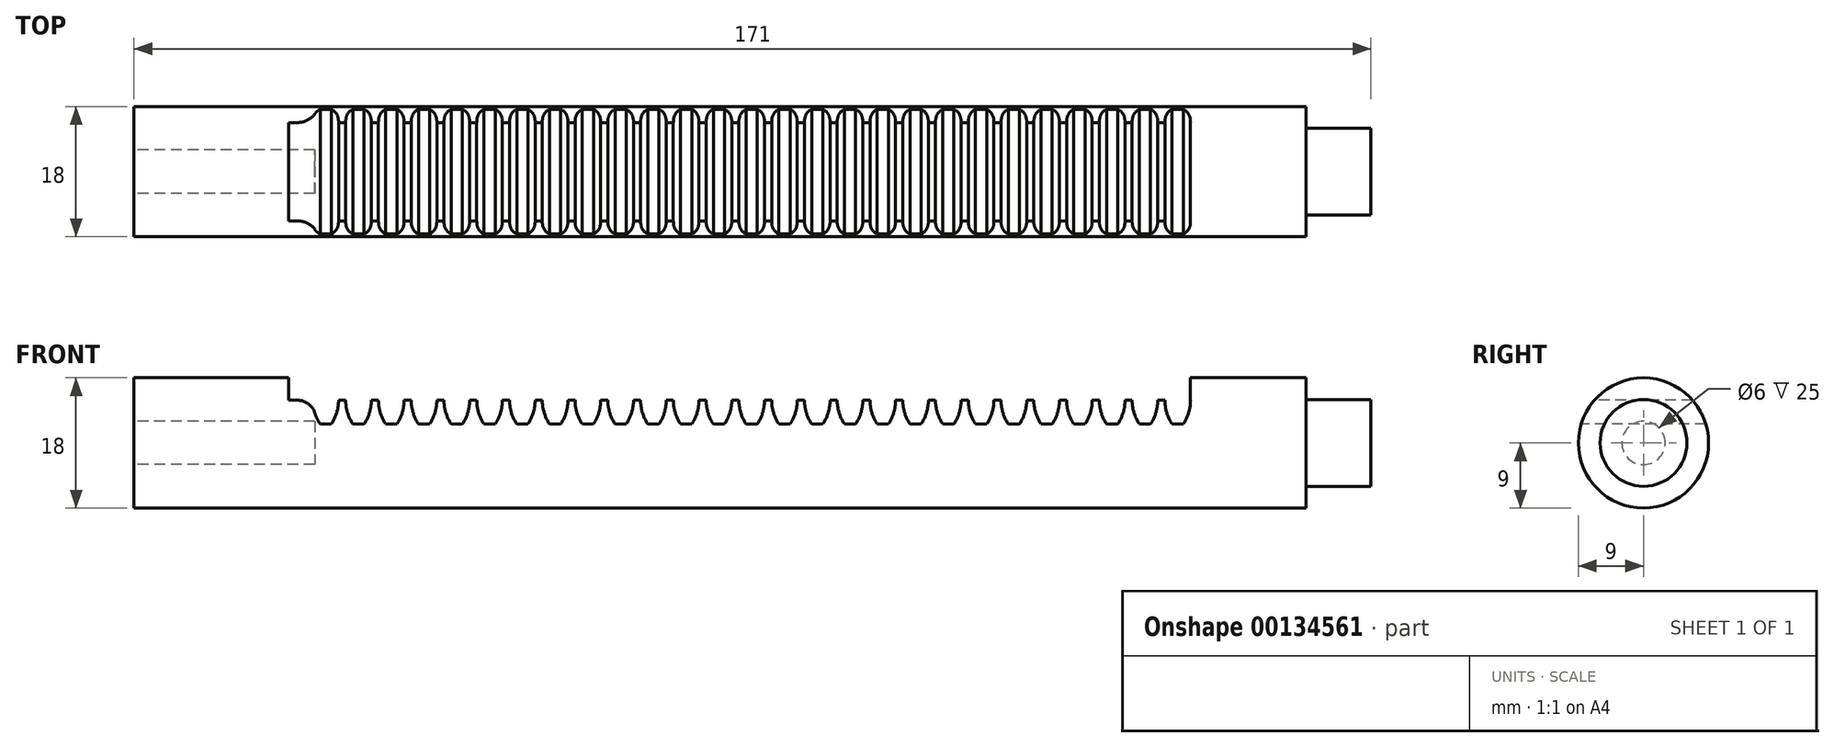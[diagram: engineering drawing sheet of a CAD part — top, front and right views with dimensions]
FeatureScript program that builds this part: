
annotation { "Feature Type Name" : "Feature", "Feature Type Description" : "" }
export const myFeature = defineFeature(function(context is Context, id is Id, definition is map)
    precondition{}
    {
        {
            var Q0;
            Q0=qCreatedBy(makeId("Right.planeOp"),FACE);
            var sketch = newSketch(context, id + "F0", { "sketchPlane" : qUnion([Q0])});
            skCircle(sketch, "E0", {"center": v(0, 0) * mm, "radius": 9 * mm});
            skSolve(sketch);
        }
        {
            var Q0;
            Q0 = qSketchRegion(id + "F0", true);
            extrude(context, id + "F1", {"entities" : qUnion([Q0]), "oppositeDirection" : true, "depth" : 162 * mm});
        }
        {
            var Q0;
            Q0=qCreatedBy(makeId("Front.planeOp"),FACE);
            var sketch = newSketch(context, id + "F2", { "sketchPlane" : qUnion([Q0])});
            skLineSegment(sketch, "E1.0", {"start": v(-162, 9) * mm, "end": v(-162, -9) * mm});
            skLineSegment(sketch, "E2", {"start": v(-162, 9) * mm, "end": v(0, 9) * mm});
            skLineSegment(sketch, "E3.0", {"start": v(0, 9) * mm, "end": v(0, -9) * mm});
            skLineSegment(sketch, "E4", {"start": v(-162, 2.6) * mm, "end": v(0, 2.6) * mm, "construction": true});
            skLineSegment(sketch, "E5", {"start": v(-162, 5.9) * mm, "end": v(0, 5.9) * mm});
            skLineSegment(sketch, "E6", {"start": v(-140.6, 5.9) * mm, "end": v(-140.6, 9) * mm});
            skPoint(sketch, "E7", {"position": v(-137.28, 5.9) * mm});
            skArc(sketch, "E8", {"start": v(-137.28, 5.9) * mm, "mid": v(-137.02, 4.18) * mm, "end": v(-136.28, 2.6) * mm});
            skLineSegment(sketch, "E9", {"start": v(-135.5, 8.15) * mm, "end": v(-135.5, -2.56) * mm, "construction": true});
            skArc(sketch, "E10.MirrorCS", {"start": v(-133.73, 5.9) * mm, "mid": v(-133.98, 4.18) * mm, "end": v(-134.73, 2.6) * mm});
            skLineSegment(sketch, "E11", {"start": v(-134.73, 2.6) * mm, "end": v(-136.28, 2.6) * mm});
            skArc(sketch, "E12.1.0.0", {"start": v(-132.75, 5.9) * mm, "mid": v(-132.49, 4.18) * mm, "end": v(-131.75, 2.6) * mm});
            skArc(sketch, "E12.1.0.1", {"start": v(-129.2, 5.9) * mm, "mid": v(-129.45, 4.18) * mm, "end": v(-130.2, 2.6) * mm});
            skArc(sketch, "E12.2.0.0", {"start": v(-128.22, 5.9) * mm, "mid": v(-127.96, 4.18) * mm, "end": v(-127.22, 2.6) * mm});
            skArc(sketch, "E12.2.0.1", {"start": v(-124.67, 5.9) * mm, "mid": v(-124.92, 4.18) * mm, "end": v(-125.67, 2.6) * mm});
            skArc(sketch, "E12.3.0.0", {"start": v(-123.69, 5.9) * mm, "mid": v(-123.43, 4.18) * mm, "end": v(-122.69, 2.6) * mm});
            skArc(sketch, "E12.3.0.1", {"start": v(-120.14, 5.9) * mm, "mid": v(-120.4, 4.18) * mm, "end": v(-121.14, 2.6) * mm});
            skArc(sketch, "E12.4.0.0", {"start": v(-119.16, 5.9) * mm, "mid": v(-118.9, 4.18) * mm, "end": v(-118.16, 2.6) * mm});
            skArc(sketch, "E12.4.0.1", {"start": v(-115.6, 5.9) * mm, "mid": v(-115.86, 4.18) * mm, "end": v(-116.6, 2.6) * mm});
            skArc(sketch, "E12.5.0.0", {"start": v(-114.63, 5.9) * mm, "mid": v(-114.37, 4.18) * mm, "end": v(-113.63, 2.6) * mm});
            skArc(sketch, "E12.5.0.1", {"start": v(-111.08, 5.9) * mm, "mid": v(-111.33, 4.18) * mm, "end": v(-112.08, 2.6) * mm});
            skArc(sketch, "E12.6.0.0", {"start": v(-110.1, 5.9) * mm, "mid": v(-109.84, 4.18) * mm, "end": v(-109.1, 2.6) * mm});
            skArc(sketch, "E12.6.0.1", {"start": v(-106.55, 5.9) * mm, "mid": v(-106.8, 4.18) * mm, "end": v(-107.55, 2.6) * mm});
            skArc(sketch, "E12.7.0.0", {"start": v(-105.57, 5.9) * mm, "mid": v(-105.3, 4.18) * mm, "end": v(-104.57, 2.6) * mm});
            skArc(sketch, "E12.7.0.1", {"start": v(-102.02, 5.9) * mm, "mid": v(-102.27, 4.18) * mm, "end": v(-103.02, 2.6) * mm});
            skArc(sketch, "E12.8.0.0", {"start": v(-101.04, 5.9) * mm, "mid": v(-100.78, 4.18) * mm, "end": v(-100.04, 2.6) * mm});
            skArc(sketch, "E12.8.0.1", {"start": v(-97.49, 5.9) * mm, "mid": v(-97.74, 4.18) * mm, "end": v(-98.49, 2.6) * mm});
            skArc(sketch, "E12.9.0.0", {"start": v(-96.5, 5.9) * mm, "mid": v(-96.25, 4.18) * mm, "end": v(-95.5, 2.6) * mm});
            skArc(sketch, "E12.9.0.1", {"start": v(-92.96, 5.9) * mm, "mid": v(-93.21, 4.18) * mm, "end": v(-93.96, 2.6) * mm});
            skArc(sketch, "E12.10.0.0", {"start": v(-91.98, 5.9) * mm, "mid": v(-91.72, 4.18) * mm, "end": v(-90.98, 2.6) * mm});
            skArc(sketch, "E12.10.0.1", {"start": v(-88.43, 5.9) * mm, "mid": v(-88.68, 4.18) * mm, "end": v(-89.43, 2.6) * mm});
            skArc(sketch, "E12.11.0.0", {"start": v(-87.45, 5.9) * mm, "mid": v(-87.19, 4.18) * mm, "end": v(-86.45, 2.6) * mm});
            skArc(sketch, "E12.11.0.1", {"start": v(-83.9, 5.9) * mm, "mid": v(-84.15, 4.18) * mm, "end": v(-84.9, 2.6) * mm});
            skArc(sketch, "E12.12.0.0", {"start": v(-82.92, 5.9) * mm, "mid": v(-82.66, 4.18) * mm, "end": v(-81.92, 2.6) * mm});
            skArc(sketch, "E12.12.0.1", {"start": v(-79.37, 5.9) * mm, "mid": v(-79.62, 4.18) * mm, "end": v(-80.37, 2.6) * mm});
            skArc(sketch, "E12.13.0.0", {"start": v(-78.39, 5.9) * mm, "mid": v(-78.13, 4.18) * mm, "end": v(-77.39, 2.6) * mm});
            skArc(sketch, "E12.13.0.1", {"start": v(-74.84, 5.9) * mm, "mid": v(-75.1, 4.18) * mm, "end": v(-75.84, 2.6) * mm});
            skArc(sketch, "E12.14.0.0", {"start": v(-73.86, 5.9) * mm, "mid": v(-73.6, 4.18) * mm, "end": v(-72.86, 2.6) * mm});
            skArc(sketch, "E12.14.0.1", {"start": v(-70.3, 5.9) * mm, "mid": v(-70.56, 4.18) * mm, "end": v(-71.3, 2.6) * mm});
            skArc(sketch, "E12.15.0.0", {"start": v(-69.33, 5.9) * mm, "mid": v(-69.07, 4.18) * mm, "end": v(-68.33, 2.6) * mm});
            skArc(sketch, "E12.15.0.1", {"start": v(-65.78, 5.9) * mm, "mid": v(-66.03, 4.18) * mm, "end": v(-66.78, 2.6) * mm});
            skArc(sketch, "E12.16.0.0", {"start": v(-64.8, 5.9) * mm, "mid": v(-64.54, 4.18) * mm, "end": v(-63.8, 2.6) * mm});
            skArc(sketch, "E12.16.0.1", {"start": v(-61.25, 5.9) * mm, "mid": v(-61.5, 4.18) * mm, "end": v(-62.25, 2.6) * mm});
            skArc(sketch, "E12.17.0.0", {"start": v(-60.27, 5.9) * mm, "mid": v(-60, 4.18) * mm, "end": v(-59.27, 2.6) * mm});
            skArc(sketch, "E12.17.0.1", {"start": v(-56.72, 5.9) * mm, "mid": v(-56.97, 4.18) * mm, "end": v(-57.72, 2.6) * mm});
            skArc(sketch, "E12.18.0.0", {"start": v(-55.74, 5.9) * mm, "mid": v(-55.48, 4.18) * mm, "end": v(-54.74, 2.6) * mm});
            skArc(sketch, "E12.18.0.1", {"start": v(-52.19, 5.9) * mm, "mid": v(-52.44, 4.18) * mm, "end": v(-53.19, 2.6) * mm});
            skArc(sketch, "E12.19.0.0", {"start": v(-51.2, 5.9) * mm, "mid": v(-50.95, 4.18) * mm, "end": v(-50.2, 2.6) * mm});
            skArc(sketch, "E12.19.0.1", {"start": v(-47.66, 5.9) * mm, "mid": v(-47.91, 4.18) * mm, "end": v(-48.66, 2.6) * mm});
            skArc(sketch, "E12.20.0.0", {"start": v(-46.68, 5.9) * mm, "mid": v(-46.42, 4.18) * mm, "end": v(-45.68, 2.6) * mm});
            skArc(sketch, "E12.20.0.1", {"start": v(-43.13, 5.9) * mm, "mid": v(-43.38, 4.18) * mm, "end": v(-44.13, 2.6) * mm});
            skArc(sketch, "E12.21.0.0", {"start": v(-42.15, 5.9) * mm, "mid": v(-41.89, 4.18) * mm, "end": v(-41.15, 2.6) * mm});
            skArc(sketch, "E12.21.0.1", {"start": v(-38.6, 5.9) * mm, "mid": v(-38.85, 4.18) * mm, "end": v(-39.6, 2.6) * mm});
            skArc(sketch, "E12.22.0.0", {"start": v(-37.62, 5.9) * mm, "mid": v(-37.36, 4.18) * mm, "end": v(-36.62, 2.6) * mm});
            skArc(sketch, "E12.22.0.1", {"start": v(-34.07, 5.9) * mm, "mid": v(-34.32, 4.18) * mm, "end": v(-35.07, 2.6) * mm});
            skArc(sketch, "E12.23.0.0", {"start": v(-33.09, 5.9) * mm, "mid": v(-32.83, 4.18) * mm, "end": v(-32.09, 2.6) * mm});
            skArc(sketch, "E12.23.0.1", {"start": v(-29.54, 5.9) * mm, "mid": v(-29.8, 4.18) * mm, "end": v(-30.54, 2.6) * mm});
            skArc(sketch, "E12.24.0.0", {"start": v(-28.56, 5.9) * mm, "mid": v(-28.3, 4.18) * mm, "end": v(-27.56, 2.6) * mm});
            skArc(sketch, "E12.24.0.1", {"start": v(-25, 5.9) * mm, "mid": v(-25.26, 4.18) * mm, "end": v(-26, 2.6) * mm});
            skArc(sketch, "E12.25.0.0", {"start": v(-24.03, 5.9) * mm, "mid": v(-23.77, 4.18) * mm, "end": v(-23.03, 2.6) * mm});
            skArc(sketch, "E12.25.0.1", {"start": v(-20.48, 5.9) * mm, "mid": v(-20.73, 4.18) * mm, "end": v(-21.48, 2.6) * mm});
            skLineSegment(sketch, "E12.direction1", {"start": v(-137.28, 5.9) * mm, "end": v(-132.75, 5.9) * mm, "construction": true});
            skLineSegment(sketch, "E13", {"start": v(-15.95, 9) * mm, "end": v(-15.95, 5.9) * mm});
            skArc(sketch, "E14.0.26.0", {"start": v(-19.5, 5.9) * mm, "mid": v(-19.24, 4.18) * mm, "end": v(-18.5, 2.6) * mm});
            skArc(sketch, "E14.4.26.0", {"start": v(-15.94, 5.9) * mm, "mid": v(-16.2, 4.18) * mm, "end": v(-16.94, 2.6) * mm});
            skLineSegment(sketch, "E15", {"start": v(-131.75, 2.6) * mm, "end": v(-130.2, 2.6) * mm});
            skLineSegment(sketch, "E16", {"start": v(-127.22, 2.6) * mm, "end": v(-125.67, 2.6) * mm});
            skLineSegment(sketch, "E17", {"start": v(-122.69, 2.6) * mm, "end": v(-121.14, 2.6) * mm});
            skLineSegment(sketch, "E18", {"start": v(-118.16, 2.6) * mm, "end": v(-116.6, 2.6) * mm});
            skLineSegment(sketch, "E19", {"start": v(-113.63, 2.6) * mm, "end": v(-112.08, 2.6) * mm});
            skLineSegment(sketch, "E20", {"start": v(-109.1, 2.6) * mm, "end": v(-107.55, 2.6) * mm});
            skLineSegment(sketch, "E21", {"start": v(-104.57, 2.6) * mm, "end": v(-103.02, 2.6) * mm});
            skLineSegment(sketch, "E22", {"start": v(-100.04, 2.6) * mm, "end": v(-98.49, 2.6) * mm});
            skLineSegment(sketch, "E23", {"start": v(-95.5, 2.6) * mm, "end": v(-93.96, 2.6) * mm});
            skLineSegment(sketch, "E24", {"start": v(-90.98, 2.6) * mm, "end": v(-89.43, 2.6) * mm});
            skLineSegment(sketch, "E25", {"start": v(-86.45, 2.6) * mm, "end": v(-84.9, 2.6) * mm});
            skLineSegment(sketch, "E26", {"start": v(-81.92, 2.6) * mm, "end": v(-80.37, 2.6) * mm});
            skLineSegment(sketch, "E27", {"start": v(-77.39, 2.6) * mm, "end": v(-75.84, 2.6) * mm});
            skLineSegment(sketch, "E28", {"start": v(-72.86, 2.6) * mm, "end": v(-71.3, 2.6) * mm});
            skLineSegment(sketch, "E29", {"start": v(-68.33, 2.6) * mm, "end": v(-66.78, 2.6) * mm});
            skLineSegment(sketch, "E30", {"start": v(-63.8, 2.6) * mm, "end": v(-62.25, 2.6) * mm});
            skLineSegment(sketch, "E31", {"start": v(-59.27, 2.6) * mm, "end": v(-57.72, 2.6) * mm});
            skLineSegment(sketch, "E32", {"start": v(-54.74, 2.6) * mm, "end": v(-53.19, 2.6) * mm});
            skLineSegment(sketch, "E33", {"start": v(-50.2, 2.6) * mm, "end": v(-48.66, 2.6) * mm});
            skLineSegment(sketch, "E34", {"start": v(-45.68, 2.6) * mm, "end": v(-44.13, 2.6) * mm});
            skLineSegment(sketch, "E35", {"start": v(-41.15, 2.6) * mm, "end": v(-39.6, 2.6) * mm});
            skLineSegment(sketch, "E36", {"start": v(-36.62, 2.6) * mm, "end": v(-35.07, 2.6) * mm});
            skLineSegment(sketch, "E37", {"start": v(-32.09, 2.6) * mm, "end": v(-30.54, 2.6) * mm});
            skLineSegment(sketch, "E38", {"start": v(-27.56, 2.6) * mm, "end": v(-26, 2.6) * mm});
            skLineSegment(sketch, "E39", {"start": v(-23.03, 2.6) * mm, "end": v(-21.48, 2.6) * mm});
            skLineSegment(sketch, "E40", {"start": v(-18.5, 2.6) * mm, "end": v(-16.94, 2.6) * mm});
            skSolve(sketch);
        }
        {
            var Q0;
            Q0 = qSketchRegion(id + "F2", true);
            extrude(context, id + "F3", {"entities" : qUnion([Q0]), "operationType" : NewBodyOperationType.REMOVE, "endBound" : BoundingType.THROUGH_ALL, "oppositeDirection" : true, "depth" : 25 * mm, "hasSecondDirection" : true, "secondDirectionBound" : SecondDirectionBoundingType.THROUGH_ALL, "secondDirectionOppositeDirection" : false, "secondDirectionDepth" : 25 * mm});
        }
        {
            var Q0;
            Q0=makeQuery(id+"F1.opExtrude","CAP_FACE",FACE,{"disambiguationData":[OSD([sQuery(id+"F0.wireOp",EDGE,"E0")])],"isStart":false});
            var sketch = newSketch(context, id + "F4", { "sketchPlane" : qUnion([Q0])});
            skLineSegment(sketch, "E41", {"start": v(0, 5.9) * mm, "end": v(0, 9) * mm, "construction": true});
            skArc(sketch, "E42", {"start": v(6.8, 5.9) * mm, "mid": v(0, 9) * mm, "end": v(-6.8, 5.9) * mm});
            skLineSegment(sketch, "E43.0", {"start": v(-6.8, 5.9) * mm, "end": v(6.8, 5.9) * mm});
            skSolve(sketch);
        }
        {
            var Q0;
            Q0 = qSketchRegion(id + "F4", true);
            extrude(context, id + "F5", {"entities" : qUnion([Q0]), "operationType" : NewBodyOperationType.ADD, "oppositeDirection" : true, "depth" : 21.4 * mm});
        }
        {
            var Q0;
            Q0=makeQuery(id+"F3.boolean.opBoolean","COPY",EDGE,{"derivedFrom":makeQuery(id+"F3.opExtrude","SWEPT_EDGE",EDGE,{"disambiguationData":[OSD([sQuery(id+"F2.wireOp",EDGE,"E5"),sQuery(id+"F2.wireOp",EDGE,"E8")])]})});
            fillet(context, id + "F6", {"entities" : qUnion([Q0]), "radius" : 2.5 * mm, "tangentPropagation" : true, "allowEdgeOverflow" : false});
        }
        {
            var Q0;
            Q0=makeQuery(id+"F1.opExtrude","CAP_FACE",FACE,{"disambiguationData":[OSD([sQuery(id+"F0.wireOp",EDGE,"E0")])],"isStart":true});
            var sketch = newSketch(context, id + "F7", { "sketchPlane" : qUnion([Q0])});
            skLineSegment(sketch, "E44", {"start": v(0, 5.9) * mm, "end": v(0, 9) * mm, "construction": true});
            skPoint(sketch, "E44.endSnap0", {"position": v(0, 5.9) * mm});
            skArc(sketch, "E45", {"start": v(6.8, 5.9) * mm, "mid": v(0, 9) * mm, "end": v(-6.8, 5.9) * mm});
            skLineSegment(sketch, "E46.1", {"start": v(6.8, 5.9) * mm, "end": v(-6.8, 5.9) * mm});
            skSolve(sketch);
        }
        {
            var Q0;
            Q0 = qSketchRegion(id + "F7", true);
            extrude(context, id + "F8", {"entities" : qUnion([Q0]), "operationType" : NewBodyOperationType.ADD, "oppositeDirection" : true, "depth" : 15.95 * mm});
        }
        {
            var Q0;
            Q0=makeQuery(id+"F5.boolean.opBoolean","MERGE",FACE,{"derivedFrom":[makeQuery(id+"F1.opExtrude","CAP_FACE",FACE,{"disambiguationData":[OSD([sQuery(id+"F0.wireOp",EDGE,"E0")])],"isStart":false}),makeQuery(id+"F5.opExtrude","CAP_FACE",FACE,{"disambiguationData":[OSD([sQuery(id+"F4.wireOp",EDGE,"E42"),sQuery(id+"F4.wireOp",EDGE,"E43.0")])],"isStart":true})]});
            var sketch = newSketch(context, id + "F9", { "sketchPlane" : qUnion([Q0])});
            skCircle(sketch, "E47", {"center": v(0, 0) * mm, "radius": 3 * mm});
            skSolve(sketch);
        }
        {
            var Q0;
            Q0 = qSketchRegion(id + "F9", true);
            extrude(context, id + "F10", {"entities" : qUnion([Q0]), "operationType" : NewBodyOperationType.REMOVE, "oppositeDirection" : true, "depth" : 25 * mm});
        }
        {
            var Q0;
            Q0=makeQuery(id+"F8.boolean.opBoolean","MERGE",FACE,{"derivedFrom":[makeQuery(id+"F1.opExtrude","CAP_FACE",FACE,{"disambiguationData":[OSD([sQuery(id+"F0.wireOp",EDGE,"E0")])],"isStart":true}),makeQuery(id+"F8.opExtrude","CAP_FACE",FACE,{"disambiguationData":[OSD([sQuery(id+"F7.wireOp",EDGE,"E45"),sQuery(id+"F7.wireOp",EDGE,"E46.1")])],"isStart":true})]});
            var sketch = newSketch(context, id + "F11", { "sketchPlane" : qUnion([Q0])});
            skCircle(sketch, "E48", {"center": v(0, 0) * mm, "radius": 6 * mm});
            skSolve(sketch);
        }
        {
            var Q0;
            Q0 = qSketchRegion(id + "F11", true);
            extrude(context, id + "F12", {"entities" : qUnion([Q0]), "operationType" : NewBodyOperationType.ADD, "depth" : 9 * mm});
        }
    });
